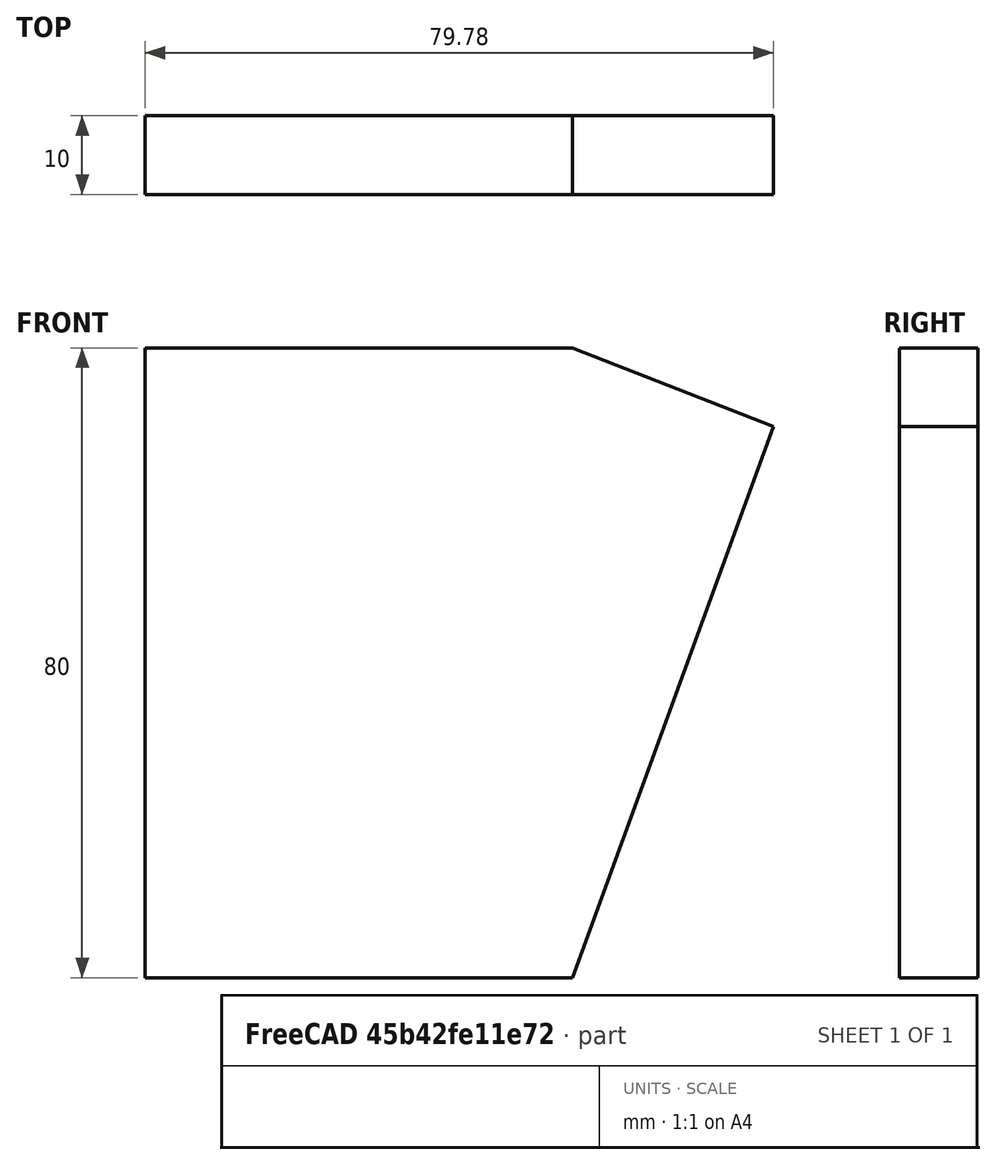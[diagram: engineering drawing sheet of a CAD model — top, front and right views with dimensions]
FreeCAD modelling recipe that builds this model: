
FCSTD DOCUMENT  (FreeCAD 0.19R24366 (Git))
Label: Tail_Hinge_Junction_Cover_Side
License: All rights reserved
LicenseURL: http://en.wikipedia.org/wiki/All_rights_reserved
objects: Sketcher::SketchObject×1, PartDesign::Pad×1, Spreadsheet::Sheet×1, PartDesign::Body×1
note: 4 computed .brp shape members not serialized (recipe doc carries the construction recipe); baked Part::Feature solids carry a one-line shape summary decoded from their .brp
EXTERNAL_REF file=../../../Master_of_Puppets.FCStd obj=Spreadsheet
EXTERNAL_REF file=../../../Master_of_Puppets.FCStd obj=Tail

FEATURE [Sketcher::SketchObject] Sketch
  FullyConstrained = true
  MapMode = 5
  Support = -> [XY_Plane001]
  expr: Constraints[18] = Spreadsheet.VerticalPlaneAngle
  expr: Constraints[16] = Spreadsheet.Width
  expr: Constraints[17] = Spreadsheet.TailHingeJunctionFullWidth
  expr: Constraints[14] = Spreadsheet.Height
  expr: Constraints[15] = Spreadsheet.Width
  sketch-geometry (7):
    g0: LineSegment StartX=0 StartY=0 StartZ=0 EndX=54.3 EndY=0 EndZ=0
    g1: LineSegment StartX=54.3 StartY=0 StartZ=0 EndX=79.7779 EndY=70 EndZ=0
    g2: LineSegment StartX=79.7779 StartY=70 StartZ=0 EndX=54.3 EndY=80 EndZ=0
    g3: LineSegment StartX=54.3 StartY=80 StartZ=0 EndX=0 EndY=80 EndZ=0
    g4: LineSegment StartX=0 StartY=80 StartZ=0 EndX=0 EndY=0 EndZ=0
    g5: LineSegment StartX=54.3 StartY=80 StartZ=0 EndX=83.4176 EndY=80 EndZ=0
    g6: LineSegment StartX=83.4176 StartY=80 StartZ=0 EndX=79.7779 EndY=70 EndZ=0
  constraints (19):
    c: Coincident(g-1,g0)
    c: PointOnObject(g0,g-1)
    c: Coincident(g0,g1)
    c: Coincident(g1,g2)
    c: Coincident(g2,g3)
    c: Horizontal(g3)
    c: Coincident(g3,g4)
    c: Vertical(g4)
    c: Coincident(g4,g-1)
    c: Coincident(g2,g5)
    c: Horizontal(g5)
    c: Coincident(g5,g6)
    c: Coincident(g6,g1)
    c: Parallel(g6,g1)
    c: Distance(g4) = 80
    c: DistanceX(g0,g0) = 54.3
    c: Distance(g3) = 54.3
    c: Distance(g1,g4) = 79.7779
    c: Angle(g1,g4) = 0.349066
FEATURE [PartDesign::Pad] Pad
  AllowMultiFace = false
  Direction = (1,1,1)
  Length = 10
  Length2 = 100
  Profile = -> Sketch
  Type = 0
  expr: Length = Spreadsheet.FlatMetalThickness
FEATURE [Spreadsheet::Sheet] Spreadsheet
  cells = A1=Inputs; A2=YawPipeDiameter; B2(YawPipeDiameter)==Master_of_Puppets#Spreadsheet.YawPipeDiameter; A3=HingeInnerPipeRadius; B3(HingeInnerPipeRadius)==Master_of_Puppets#Tail.HingeInnerPipeRadius; A4=VerticalPlaneAngle; B4(VerticalPlaneAngle)==Master_of_Puppets#Spreadsheet.VerticalPlaneAngle; A5=FlatMetalThickness; B5(FlatMetalThickness)==Master_of_Puppets#Spreadsheet.FlatMetalThickness; A6=Height; B6(Height)==Master_of_Puppets#Tail.TailHingeJunctionHeight; A7=TailHingeJunctionFullWidth; B7(TailHingeJunctionFullWidth)==Master_of_Puppets#Tail.TailHingeJunctionFullWidth; A8=Calculated; A9=YawPipeRadius; B9(YawPipeRadius)==YawPipeDiameter / 2; A10=Width; B10(Width)==YawPipeRadius + HingeInnerPipeRadius
FEATURE [PartDesign::Body] PadBody  label="Tail_Hinge_Junction_Cover_Side"
  Group = -> [Sketch,Pad]
  Openafpm_Flat = true
  Origin = -> Origin001
  Placement = pos=(0,0,0) rot=(1,0,0;1.5708rad)
  Tip = -> Pad
